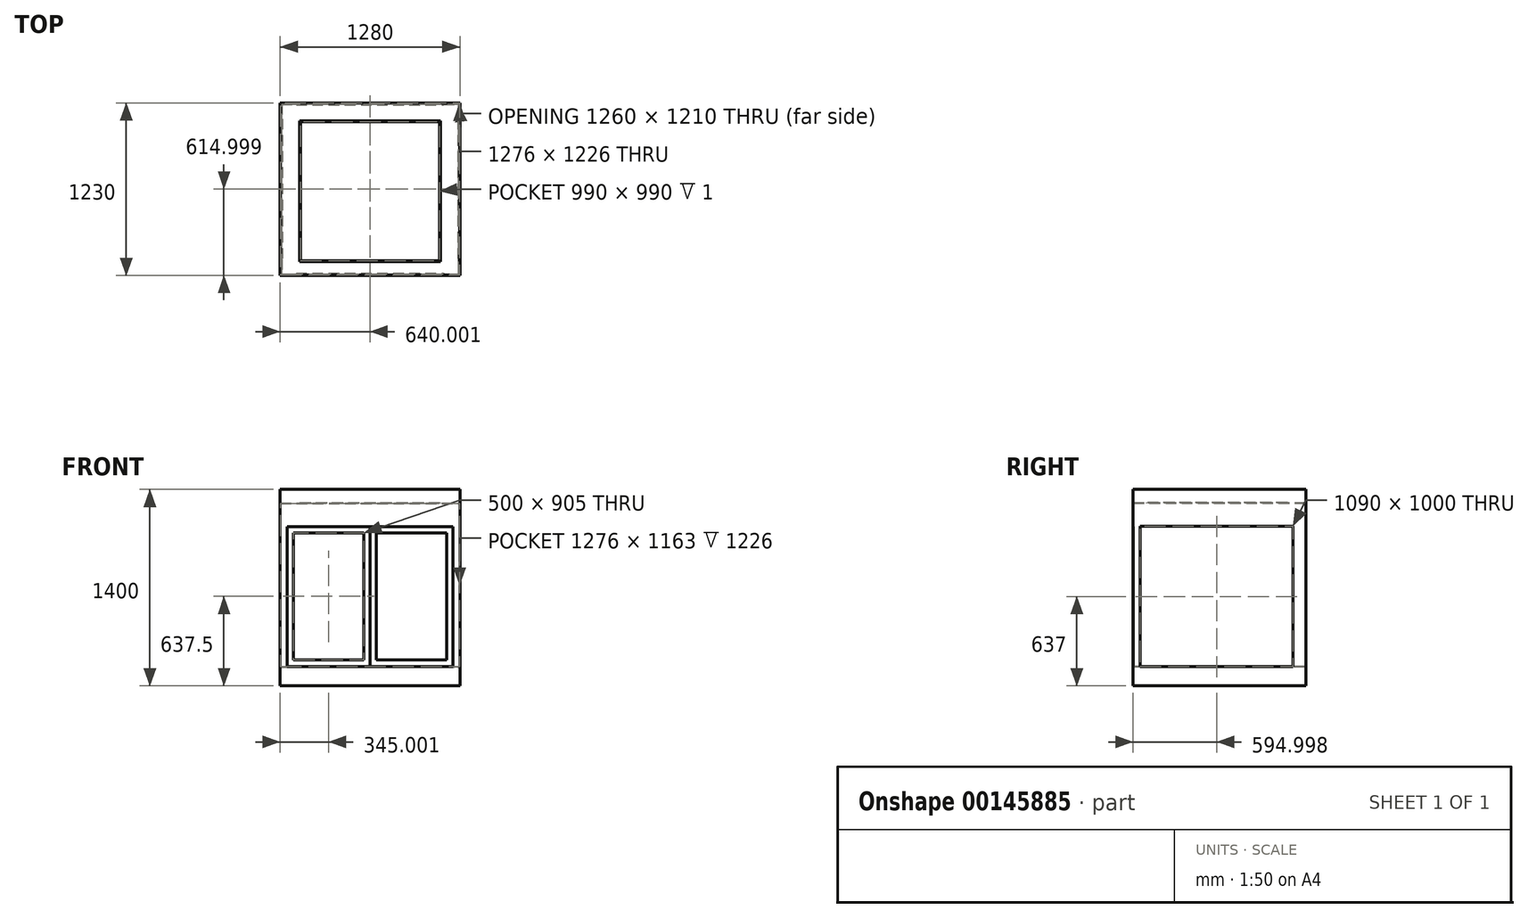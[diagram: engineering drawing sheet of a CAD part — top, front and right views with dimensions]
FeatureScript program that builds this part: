
annotation { "Feature Type Name" : "Feature", "Feature Type Description" : "" }
export const myFeature = defineFeature(function(context is Context, id is Id, definition is map)
    precondition{}
    {
        {
            var Q0;
            Q0=qCreatedBy(makeId("Top.planeOp"),FACE);
            var sketch = newSketch(context, id + "F0", { "sketchPlane" : qUnion([Q0])});
            skLineSegment(sketch, "E0.bottom", {"start": v(-1207.65, 1124.38) * mm, "end": v(52.35, 1124.38) * mm});
            skLineSegment(sketch, "E0.top", {"start": v(-1207.65, -85.62) * mm, "end": v(52.35, -85.62) * mm});
            skLineSegment(sketch, "E0.left", {"start": v(-1207.65, 1124.38) * mm, "end": v(-1207.65, -85.62) * mm});
            skLineSegment(sketch, "E0.right", {"start": v(52.35, 1124.38) * mm, "end": v(52.35, -85.62) * mm});
            skLineSegment(sketch, "E1.0", {"start": v(-1202.65, 1119.38) * mm, "end": v(47.35, 1119.38) * mm});
            skLineSegment(sketch, "E2.0", {"start": v(-1202.65, 1119.38) * mm, "end": v(-1202.65, -80.62) * mm});
            skLineSegment(sketch, "E2.1", {"start": v(-1202.65, -80.62) * mm, "end": v(47.35, -80.62) * mm});
            skLineSegment(sketch, "E2.2", {"start": v(47.35, 1119.38) * mm, "end": v(47.35, -80.62) * mm});
            skLineSegment(sketch, "E3.0", {"start": v(-1190.15, 1106.88) * mm, "end": v(34.85, 1106.88) * mm});
            skLineSegment(sketch, "E3.1", {"start": v(-1190.15, 1106.88) * mm, "end": v(-1190.15, -68.12) * mm});
            skLineSegment(sketch, "E3.2", {"start": v(-1190.15, -68.12) * mm, "end": v(34.85, -68.12) * mm});
            skLineSegment(sketch, "E3.3", {"start": v(34.85, 1106.88) * mm, "end": v(34.85, -68.12) * mm});
            skLineSegment(sketch, "E4.0", {"start": v(-1217.65, 1134.38) * mm, "end": v(62.35, 1134.38) * mm});
            skLineSegment(sketch, "E4.1", {"start": v(-1217.65, 1134.38) * mm, "end": v(-1217.65, -95.62) * mm});
            skLineSegment(sketch, "E4.2", {"start": v(-1217.65, -95.62) * mm, "end": v(62.35, -95.62) * mm});
            skLineSegment(sketch, "E4.3", {"start": v(62.35, 1134.38) * mm, "end": v(62.35, -95.62) * mm});
            skLineSegment(sketch, "E5.0", {"start": v(-1102.65, 1124.38) * mm, "end": v(-1102.65, -85.62) * mm});
            skLineSegment(sketch, "E6.0", {"start": v(-52.65, 1124.38) * mm, "end": v(-52.65, -85.62) * mm});
            skLineSegment(sketch, "E7.0", {"start": v(-1207.65, 1019.38) * mm, "end": v(52.35, 1019.38) * mm});
            skLineSegment(sketch, "E8.0", {"start": v(-1207.65, 19.38) * mm, "end": v(52.35, 19.38) * mm});
            skLineSegment(sketch, "E9.0", {"start": v(-1215.65, 1132.38) * mm, "end": v(60.35, 1132.38) * mm});
            skLineSegment(sketch, "E9.1", {"start": v(-1215.65, 1132.38) * mm, "end": v(-1215.65, -93.62) * mm});
            skLineSegment(sketch, "E9.2", {"start": v(-1215.65, -93.62) * mm, "end": v(60.35, -93.62) * mm});
            skLineSegment(sketch, "E9.3", {"start": v(60.35, 1132.38) * mm, "end": v(60.35, -93.62) * mm});
            skSolve(sketch);
        }
        {
            var Q0;
            Q0=makeQuery(id+"F0.imprint","IMPRINT",FACE,{"disambiguationData":[TD([[makeQuery(id+"F0.imprint","IMPRINT",EDGE,{"derivedFrom":sQuery(id+"F0.wireOp",EDGE,"E4.0")}),-1.0]])]});
            extrude(context, id + "F1", {"entities" : qUnion([Q0]), "depth" : 1165 * mm});
        }
        {
            var Q0;
            Q0=makeQuery(id+"F0.imprint","IMPRINT",FACE,{"disambiguationData":[TD([[makeQuery(id+"F0.imprint","IMPRINT",EDGE,{"derivedFrom":sQuery(id+"F0.wireOp",EDGE,"E9.0")}),-1.0]])]});
            var Q1;
            {var subQ0=sQuery(id+"F0.wireOp",EDGE,"E5.0");var subQ1=sQuery(id+"F0.wireOp",EDGE,"E0.bottom");var subQ2=makeQuery(id+"F0.imprint","INTERSECT",VERTEX,{"derivedFrom":[subQ1,subQ0]});Q1=makeQuery(id+"F0.imprint","IMPRINT",FACE,{"disambiguationData":[TD([[makeQuery(id+"F0.imprint","IMPRINT",EDGE,{"disambiguationData":[TD([[subQ2,-1.0]])],"derivedFrom":subQ1}),-1.0]])]});}
            var Q2;
            {var subQ0=sQuery(id+"F0.wireOp",EDGE,"E7.0");var subQ1=sQuery(id+"F0.wireOp",EDGE,"E0.left");var subQ2=makeQuery(id+"F0.imprint","INTERSECT",VERTEX,{"derivedFrom":[subQ1,subQ0]});Q2=makeQuery(id+"F0.imprint","IMPRINT",FACE,{"disambiguationData":[TD([[makeQuery(id+"F0.imprint","IMPRINT",EDGE,{"disambiguationData":[TD([[subQ2,-1.0]])],"derivedFrom":subQ1}),1.0]])]});}
            var Q3;
            {var subQ0=sQuery(id+"F0.wireOp",EDGE,"E5.0");var subQ1=sQuery(id+"F0.wireOp",EDGE,"E0.top");var subQ2=makeQuery(id+"F0.imprint","INTERSECT",VERTEX,{"derivedFrom":[subQ1,subQ0]});Q3=makeQuery(id+"F0.imprint","IMPRINT",FACE,{"disambiguationData":[TD([[makeQuery(id+"F0.imprint","IMPRINT",EDGE,{"disambiguationData":[TD([[subQ2,-1.0]])],"derivedFrom":subQ1}),1.0]])]});}
            var Q4;
            {var subQ0=sQuery(id+"F0.wireOp",EDGE,"E7.0");var subQ1=sQuery(id+"F0.wireOp",EDGE,"E0.right");var subQ2=makeQuery(id+"F0.imprint","INTERSECT",VERTEX,{"derivedFrom":[subQ1,subQ0]});Q4=makeQuery(id+"F0.imprint","IMPRINT",FACE,{"disambiguationData":[TD([[makeQuery(id+"F0.imprint","IMPRINT",EDGE,{"disambiguationData":[TD([[subQ2,-1.0]])],"derivedFrom":subQ1}),-1.0]])]});}
            extrude(context, id + "F2", {"entities" : qUnion([Q0, Q1, Q2, Q3, Q4]), "operationType" : NewBodyOperationType.ADD, "depth" : 2 * mm});
        }
        {
            var Q0;
            Q0=makeQuery(id+"F0.imprint","IMPRINT",FACE,{"disambiguationData":[TD([[makeQuery(id+"F0.imprint","IMPRINT",EDGE,{"derivedFrom":sQuery(id+"F0.wireOp",EDGE,"E4.0")}),-1.0]])]});
            extrude(context, id + "F3", {"entities" : qUnion([Q0]), "operationType" : NewBodyOperationType.ADD, "oppositeDirection" : true, "depth" : 135 * mm});
        }
        {
            var Q0;
            {var subQ0=sQuery(id+"F0.wireOp",EDGE,"E4.2");Q0=makeQuery(id+"F3.boolean.opBoolean","MERGE",FACE,{"derivedFrom":[makeQuery(id+"F1.opExtrude","SWEPT_FACE",FACE,{"disambiguationData":[OSD([subQ0])]}),makeQuery(id+"F3.opExtrude","SWEPT_FACE",FACE,{"disambiguationData":[OSD([subQ0])]})]});}
            var sketch = newSketch(context, id + "F4", { "sketchPlane" : qUnion([Q0])});
            skLineSegment(sketch, "E10.bottom", {"start": v(-37.65, -115) * mm, "end": v(-187.65, -115) * mm});
            skLineSegment(sketch, "E10.top", {"start": v(-37.65, -65) * mm, "end": v(-187.65, -65) * mm});
            skLineSegment(sketch, "E10.left", {"start": v(-37.65, -115) * mm, "end": v(-37.65, -65) * mm});
            skLineSegment(sketch, "E10.right", {"start": v(-187.65, -115) * mm, "end": v(-187.65, -65) * mm});
            skLineSegment(sketch, "E11.0", {"start": v(-1217.65, 0) * mm, "end": v(62.35, 0) * mm});
            skLineSegment(sketch, "E12.0", {"start": v(-1217.65, -25) * mm, "end": v(62.35, -25) * mm});
            skLineSegment(sketch, "E13.0", {"start": v(-1167.65, 1000) * mm, "end": v(12.35, 1000) * mm});
            skLineSegment(sketch, "E14.0", {"start": v(-1167.65, 1000) * mm, "end": v(-1167.65, 0) * mm});
            skLineSegment(sketch, "E15.0", {"start": v(12.35, 1000) * mm, "end": v(12.35, 0) * mm});
            skLineSegment(sketch, "E16.0", {"start": v(-32.65, 955) * mm, "end": v(-32.65, 50) * mm});
            skLineSegment(sketch, "E17.0", {"start": v(-1122.65, 955) * mm, "end": v(-1122.65, 50) * mm});
            skLineSegment(sketch, "E18.0", {"start": v(-622.65, 955) * mm, "end": v(-622.65, 50) * mm});
            skLineSegment(sketch, "E19.0", {"start": v(-532.65, 955) * mm, "end": v(-532.65, 50) * mm});
            skLineSegment(sketch, "E20.0", {"start": v(-577.65, 1000) * mm, "end": v(-577.65, -135) * mm});
            skLineSegment(sketch, "E21.0", {"start": v(-1122.65, 955) * mm, "end": v(-622.65, 955) * mm});
            skLineSegment(sketch, "E22.0", {"start": v(-1122.65, 50) * mm, "end": v(-622.65, 50) * mm});
            skLineSegment(sketch, "E23.trimOffspring", {"start": v(-532.65, 955) * mm, "end": v(-32.65, 955) * mm});
            skLineSegment(sketch, "E24.trimOffspring", {"start": v(-532.65, 50) * mm, "end": v(-32.65, 50) * mm});
            skLineSegment(sketch, "E25.0", {"start": v(-1215.65, 0) * mm, "end": v(60.35, 0) * mm});
            skLineSegment(sketch, "E26.0", {"start": v(-1215.65, 2) * mm, "end": v(60.35, 2) * mm});
            skSolve(sketch);
        }
        {
            var Q0;
            Q0=makeQuery(id+"F1.opExtrude","CAP_FACE",FACE,{"disambiguationData":[OSD([sQuery(id+"F0.wireOp",EDGE,"E4.0"),sQuery(id+"F0.wireOp",EDGE,"E4.1"),sQuery(id+"F0.wireOp",EDGE,"E4.2"),sQuery(id+"F0.wireOp",EDGE,"E4.3"),sQuery(id+"F0.wireOp",EDGE,"E9.0"),sQuery(id+"F0.wireOp",EDGE,"E9.1"),sQuery(id+"F0.wireOp",EDGE,"E9.2"),sQuery(id+"F0.wireOp",EDGE,"E9.3")])],"isStart":false});
            var sketch = newSketch(context, id + "F5", { "sketchPlane" : qUnion([Q0])});
            skLineSegment(sketch, "E27.0", {"start": v(-1217.65, 1134.38) * mm, "end": v(62.35, 1134.38) * mm});
            skLineSegment(sketch, "E27.1", {"start": v(-1215.65, 1132.38) * mm, "end": v(60.35, 1132.38) * mm});
            skLineSegment(sketch, "E27.2", {"start": v(62.35, 1134.38) * mm, "end": v(62.35, -95.62) * mm});
            skLineSegment(sketch, "E27.3", {"start": v(60.35, 1132.38) * mm, "end": v(60.35, -93.62) * mm});
            skLineSegment(sketch, "E27.4", {"start": v(-1217.65, 1134.38) * mm, "end": v(-1217.65, -95.62) * mm});
            skLineSegment(sketch, "E27.5", {"start": v(-1215.65, 1132.38) * mm, "end": v(-1215.65, -93.62) * mm});
            skLineSegment(sketch, "E27.6", {"start": v(-1215.65, -93.62) * mm, "end": v(60.35, -93.62) * mm});
            skLineSegment(sketch, "E27.7", {"start": v(-1217.65, -95.62) * mm, "end": v(62.35, -95.62) * mm});
            skLineSegment(sketch, "E28.0", {"start": v(-1077.65, 1004.38) * mm, "end": v(-1077.65, 4.38) * mm});
            skLineSegment(sketch, "E29.0", {"start": v(-77.65, 1004.38) * mm, "end": v(-77.65, 4.38) * mm});
            skLineSegment(sketch, "E30.0", {"start": v(-1077.65, 1004.38) * mm, "end": v(-77.65, 1004.38) * mm});
            skLineSegment(sketch, "E31.0", {"start": v(-1077.65, 4.38) * mm, "end": v(-77.65, 4.38) * mm});
            skSolve(sketch);
        }
        {
            var Q0;
            Q0=makeQuery(id+"F5.imprint","IMPRINT",FACE,{"disambiguationData":[TD([[makeQuery(id+"F5.imprint","IMPRINT",EDGE,{"derivedFrom":sQuery(id+"F5.wireOp",EDGE,"E27.0")}),-1.0]])]});
            extrude(context, id + "F6", {"entities" : qUnion([Q0]), "depth" : 100 * mm});
        }
        {
            var Q0;
            Q0=makeQuery(id+"F5.imprint","IMPRINT",FACE,{"disambiguationData":[TD([[makeQuery(id+"F5.imprint","IMPRINT",EDGE,{"derivedFrom":sQuery(id+"F5.wireOp",EDGE,"E27.1")}),-1.0]])]});
            extrude(context, id + "F7", {"entities" : qUnion([Q0]), "operationType" : NewBodyOperationType.ADD, "depth" : 6 * mm});
        }
        {
            var Q0;
            Q0=makeQuery(id+"F5.imprint","IMPRINT",FACE,{"disambiguationData":[TD([[makeQuery(id+"F5.imprint","IMPRINT",EDGE,{"derivedFrom":sQuery(id+"F5.wireOp",EDGE,"E28.0")}),1.0]])]});
            extrude(context, id + "F8", {"entities" : qUnion([Q0]), "depth" : 5 * mm});
        }
        {
            var Q0;
            Q0=makeQuery(id+"F7.opExtrude","CAP_FACE",FACE,{"disambiguationData":[OSD([sQuery(id+"F5.wireOp",EDGE,"E27.1"),sQuery(id+"F5.wireOp",EDGE,"E27.3"),sQuery(id+"F5.wireOp",EDGE,"E27.5"),sQuery(id+"F5.wireOp",EDGE,"E27.6"),sQuery(id+"F5.wireOp",EDGE,"E28.0"),sQuery(id+"F5.wireOp",EDGE,"E29.0"),sQuery(id+"F5.wireOp",EDGE,"E30.0"),sQuery(id+"F5.wireOp",EDGE,"E31.0")])],"isStart":false});
            var sketch = newSketch(context, id + "F9", { "sketchPlane" : qUnion([Q0])});
            skLineSegment(sketch, "E32.0", {"start": v(-1072.65, 999.38) * mm, "end": v(-82.65, 999.38) * mm});
            skLineSegment(sketch, "E32.1", {"start": v(-1072.65, 999.38) * mm, "end": v(-1072.65, 9.38) * mm});
            skLineSegment(sketch, "E32.2", {"start": v(-1072.65, 9.38) * mm, "end": v(-82.65, 9.38) * mm});
            skLineSegment(sketch, "E32.3", {"start": v(-82.65, 999.38) * mm, "end": v(-82.65, 9.38) * mm});
            skLineSegment(sketch, "E33.0", {"start": v(-1079.65, 1006.38) * mm, "end": v(-1079.65, 2.38) * mm});
            skLineSegment(sketch, "E33.1", {"start": v(-1079.65, 1006.38) * mm, "end": v(-75.65, 1006.38) * mm});
            skLineSegment(sketch, "E33.2", {"start": v(-75.65, 1006.38) * mm, "end": v(-75.65, 2.38) * mm});
            skLineSegment(sketch, "E33.3", {"start": v(-1079.65, 2.38) * mm, "end": v(-75.65, 2.38) * mm});
            skSolve(sketch);
        }
        {
            var Q0;
            Q0=makeQuery(id+"F9.imprint","IMPRINT",FACE,{"disambiguationData":[TD([[makeQuery(id+"F9.imprint","IMPRINT",EDGE,{"derivedFrom":sQuery(id+"F9.wireOp",EDGE,"E33.0")}),-1.0]])]});
            extrude(context, id + "F10", {"entities" : qUnion([Q0]), "operationType" : NewBodyOperationType.REMOVE, "oppositeDirection" : true, "depth" : 4 * mm});
        }
        {
            var Q0;
            Q0=makeQuery(id+"F9.imprint","IMPRINT",FACE,{"disambiguationData":[TD([[makeQuery(id+"F9.imprint","IMPRINT",EDGE,{"derivedFrom":sQuery(id+"F9.wireOp",EDGE,"E32.0")}),1.0]])]});
            extrude(context, id + "F11", {"entities" : qUnion([Q0]), "operationType" : NewBodyOperationType.ADD, "oppositeDirection" : true, "depth" : 1 * mm});
        }
        {
            var Q0;
            Q0=makeQuery(id+"F4.imprint","IMPRINT",FACE,{"disambiguationData":[TD([[makeQuery(id+"F4.imprint","IMPRINT",EDGE,{"derivedFrom":sQuery(id+"F4.wireOp",EDGE,"E17.0")}),-1.0]])]});
            var Q1;
            Q1=makeQuery(id+"F4.imprint","IMPRINT",FACE,{"disambiguationData":[TD([[makeQuery(id+"F4.imprint","IMPRINT",EDGE,{"derivedFrom":sQuery(id+"F4.wireOp",EDGE,"E16.0")}),1.0]])]});
            extrude(context, id + "F12", {"entities" : qUnion([Q0, Q1]), "operationType" : NewBodyOperationType.REMOVE, "oppositeDirection" : true, "depth" : 25 * mm});
        }
        {
            var Q0;
            Q0=makeQuery(id+"F4.imprint","IMPRINT",FACE,{"disambiguationData":[TD([[makeQuery(id+"F4.imprint","IMPRINT",EDGE,{"derivedFrom":sQuery(id+"F4.wireOp",EDGE,"E17.0")}),-1.0]])]});
            extrude(context, id + "F13", {"entities" : qUnion([Q0]), "oppositeDirection" : true, "depth" : 6 * mm});
        }
        {
            var Q0;
            Q0=makeQuery(id+"F13.opExtrude","CAP_FACE",FACE,{"disambiguationData":[OSD([sQuery(id+"F4.wireOp",EDGE,"E13.0"),sQuery(id+"F4.wireOp",EDGE,"E14.0"),sQuery(id+"F4.wireOp",EDGE,"E17.0"),sQuery(id+"F4.wireOp",EDGE,"E18.0"),sQuery(id+"F4.wireOp",EDGE,"E20.0"),sQuery(id+"F4.wireOp",EDGE,"E21.0"),sQuery(id+"F4.wireOp",EDGE,"E22.0"),sQuery(id+"F4.wireOp",EDGE,"E26.0")])],"isStart":false});
            var sketch = newSketch(context, id + "F14", { "sketchPlane" : qUnion([Q0])});
            skLineSegment(sketch, "E34.0", {"start": v(579.65, 998) * mm, "end": v(1165.65, 998) * mm});
            skLineSegment(sketch, "E34.1", {"start": v(1165.65, 4) * mm, "end": v(1165.65, 998) * mm});
            skLineSegment(sketch, "E34.2", {"start": v(579.65, 4) * mm, "end": v(1165.65, 4) * mm});
            skLineSegment(sketch, "E34.3", {"start": v(579.65, 4) * mm, "end": v(579.65, 998) * mm});
            skLineSegment(sketch, "E35.0", {"start": v(1124.65, 48) * mm, "end": v(1124.65, 957) * mm});
            skLineSegment(sketch, "E35.1", {"start": v(620.65, 48) * mm, "end": v(1124.65, 48) * mm});
            skLineSegment(sketch, "E35.2", {"start": v(620.65, 48) * mm, "end": v(620.65, 957) * mm});
            skLineSegment(sketch, "E35.3", {"start": v(620.65, 957) * mm, "end": v(1124.65, 957) * mm});
            skSolve(sketch);
        }
        {
            var Q0;
            Q0=makeQuery(id+"F14.imprint","IMPRINT",FACE,{"disambiguationData":[TD([[makeQuery(id+"F14.imprint","IMPRINT",EDGE,{"derivedFrom":sQuery(id+"F14.wireOp",EDGE,"E34.0")}),-1.0]])]});
            extrude(context, id + "F15", {"entities" : qUnion([Q0]), "operationType" : NewBodyOperationType.REMOVE, "oppositeDirection" : true, "depth" : 4 * mm});
        }
        {
            var Q0;
            {var subQ0=sQuery(id+"F0.wireOp",EDGE,"E4.1");Q0=makeQuery(id+"F3.boolean.opBoolean","MERGE",FACE,{"derivedFrom":[makeQuery(id+"F1.opExtrude","SWEPT_FACE",FACE,{"disambiguationData":[OSD([subQ0])]}),makeQuery(id+"F3.opExtrude","SWEPT_FACE",FACE,{"disambiguationData":[OSD([subQ0])]})]});}
            var sketch = newSketch(context, id + "F16", { "sketchPlane" : qUnion([Q0])});
            skLineSegment(sketch, "E36.0", {"start": v(-1132.38, 2) * mm, "end": v(93.62, 2) * mm});
            skLineSegment(sketch, "E37.0", {"start": v(-999.38, 47) * mm, "end": v(0.62, 47) * mm});
            skLineSegment(sketch, "E38.0", {"start": v(-999.38, 957) * mm, "end": v(0.62, 957) * mm});
            skLineSegment(sketch, "E39.0", {"start": v(-1132.38, 1002) * mm, "end": v(93.62, 1002) * mm});
            skLineSegment(sketch, "E40.0", {"start": v(45.62, 1002) * mm, "end": v(45.62, 2) * mm});
            skLineSegment(sketch, "E41.0", {"start": v(0.62, 957) * mm, "end": v(0.62, 47) * mm});
            skLineSegment(sketch, "E42.0", {"start": v(-999.38, 957) * mm, "end": v(-999.38, 47) * mm});
            skLineSegment(sketch, "E43.0", {"start": v(-1044.38, 1002) * mm, "end": v(-1044.38, 2) * mm});
            skSolve(sketch);
        }
        {
            var Q0;
            Q0=makeQuery(id+"F16.imprint","IMPRINT",FACE,{"disambiguationData":[TD([[makeQuery(id+"F16.imprint","IMPRINT",EDGE,{"derivedFrom":sQuery(id+"F16.wireOp",EDGE,"E37.0")}),-1.0]])]});
            extrude(context, id + "F17", {"entities" : qUnion([Q0]), "operationType" : NewBodyOperationType.REMOVE, "oppositeDirection" : true, "depth" : 25 * mm});
        }
        {
            var Q0;
            Q0=makeQuery(id+"F16.imprint","IMPRINT",FACE,{"disambiguationData":[TD([[makeQuery(id+"F16.imprint","IMPRINT",EDGE,{"derivedFrom":sQuery(id+"F16.wireOp",EDGE,"E37.0")}),-1.0]])]});
            var Q1;
            Q1=makeQuery(id+"F16.imprint","IMPRINT",FACE,{"disambiguationData":[TD([[makeQuery(id+"F16.imprint","IMPRINT",EDGE,{"derivedFrom":sQuery(id+"F16.wireOp",EDGE,"E37.0")}),1.0]])]});
            extrude(context, id + "F18", {"entities" : qUnion([Q0, Q1]), "operationType" : NewBodyOperationType.REMOVE, "oppositeDirection" : true, "depth" : 1500 * mm});
        }
    });
